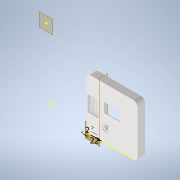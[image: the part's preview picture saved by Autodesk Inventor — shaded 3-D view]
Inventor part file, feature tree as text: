
AUTODESK INVENTOR PART (.ipt)
format: ipt  version: 2022.2 (Build 262287010, 287A)  size: 574,976 bytes
history: native  units: mm
features: sketch x19, extrude x17, plane x6, projected_geometry x1
ambient origin geometry x8: Origin, YZ Plane, XZ Plane, XY Plane, X Axis, Y Axis, Z Axis, Center Point
bodies: Volumenkörper1 (feature_tree)
feature tree (43):
  plane  "Arbeitsebene1"
  extrude  "Extrusion1"  Depth=2.0mm
  extrude  "Extrusion2"  Depth=24.0mm
  extrude  "Extrusion3"  Depth=71.8mm
  extrude  "Extrusion4"  Depth=22.0mm
  extrude  "Extrusion5"  Depth=2.0mm
  sketch  "Skizze6"  dims[d16=9.0mm d17=0.0mm d18=1.6mm]
  plane  "Arbeitsebene2"
  extrude  "Extrusion8"  Depth=1.6mm
  plane  "Arbeitsebene4"
  extrude  "Extrusion9"  Depth=7.3mm
  plane  "Arbeitsebene3"
  extrude  "Extrusion10"  Depth=25.0mm
  plane  "Arbeitsebene5"
  extrude  "Extrusion11"  Depth=2.75mm TaperAngle=0.0deg
  plane  "Arbeitsebene6"
  extrude  "Extrusion12"  Depth=2.0mm
  extrude  "Extrusion13"  Depth=2.0mm
  extrude  "Extrusion14"  Depth=16.0mm
  extrude  "Extrusion15"  Depth=1.0mm
  extrude  "Extrusion16"  Depth=10.0mm TaperAngle=0.0deg
  sketch  "Skizze18"  dims[d52=70.0mm d54=2.4mm d55=10.0mm d57=10.0mm d59=1.4mm d60=0.0mm]
  extrude  "Extrusion17"  Depth=1.2mm
  extrude  "Extrusion18"  Depth=1.4mm TaperAngle=0.0deg
  extrude  "Extrusion19"  Depth=3.0mm
  sketch  "Skizze21"  dims[d71=2.0mm d72=0.0mm d73=0.0mm d74=2.9mm d75=0.0mm d76=2.0mm d77=27.0mm d78=0.0mm d79=7.0mm d80=27.0mm d81=3.5mm d82=0.0mm d83=3.5mm d84=0.0mm d85=2.0mm d86=3.5mm d87=0.0mm d88=12.0mm d89=2.5mm d90=4.0mm d91=7.6mm d92=1.4mm d93=0.0mm d94=1.0mm d95=0.0mm d96=3.0mm d97=3.0mm d98=1.0mm d99=0.0mm d100=3.0mm d101=3.0mm d102=22.0mm]
  sketch  "Skizze1"  dims[d0=9.0mm d2=2.0mm]
  sketch  "Skizze2"  dims[d3=7.5mm d6=24.0mm]
  sketch  "Skizze3"  dims[d7=14.0mm d8=71.8mm]
  sketch  "Skizze4"  dims[d9=23.9mm d10=22.0mm]
  sketch  "Skizze5"  dims[d13=2.0mm d14=0.0mm d15=2.0mm]
  projected_geometry  "Projizierte Kontur1"
  sketch  "Skizze9"  dims[d19=18.3mm d20=7.3mm]
  sketch  "Skizze10"  dims[d21=51.75mm d22=24.0mm d23=0.0mm d24=0.0mm d25=25.0mm]
  sketch  "Skizze11"  dims[d26=26.0mm d27=2.75mm d28=0.0mm]
  sketch  "Skizze12"  dims[d29=2.0mm d30=2.0mm]
  sketch  "Skizze13"  dims[d31=2.75mm d32=0.0mm d33=2.0mm]
  sketch  "Skizze14"  dims[d41=10.0mm d42=0.0mm d43=16.0mm]
  sketch  "Skizze15"  dims[d44=23.0mm d45=1.0mm]
  sketch  "Skizze16"  dims[d46=2.0mm d47=0.0mm d48=10.0mm d49=0.0mm]
  sketch  "Skizze17"  dims[d50=1.2mm d51=1.2mm]
  sketch  "Skizze19"  dims[d61=1.2mm d62=70.0mm d64=3.0mm d65=10.0mm d67=10.0mm]
  sketch  "Skizze20"  dims[d69=1.4mm d70=0.0mm]
